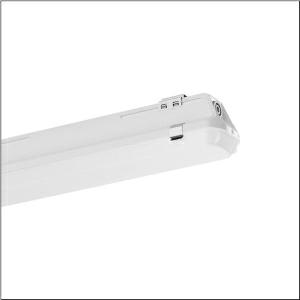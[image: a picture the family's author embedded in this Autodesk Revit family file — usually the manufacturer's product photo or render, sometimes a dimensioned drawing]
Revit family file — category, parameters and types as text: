
# Revit family: monsun_r__11_emergency_51fp20dp467h3h_e354
name_source: partatom
category: Lighting Fixtures
units: mm (PartAtom-declared; Revit-internal decimal feet)

## family parameters
Cut with Voids When Loaded = No
Host = Face
Light Source = No
Part Type = Normal
Room Calculation Point = No
Round Connector Dimension = Use Diameter
Shared = No

## types (1)
- --- (1 x LED, 790 lm, 5 W, 4000K)
    Apparent Load = 5 VA
    CIE Flux Codes = 45 75 93 94 100
    Color Rendering = 80
    Color Temperature = 4000K
    Default Elevation = 1800 mm
    Description = Monsun® 11 emergency, damp-proof luminaire, chain hanger, primary optical cover: enclosure, of PC, light emission: direct distribution, primary light characteristic: symmetric, installation type: suspended mounting, surface-mounted, horizontal mounting, vertical mounting, LED, rated luminous flux: 5.450lm, luminous efficacy: 158lm/W, light colour: 840, colour temperature: 4000K, control gear: ECG DALI, with terminal, 5+3-pole, max. 2.5mm², mains connection: 220..240V, AC, 50/60Hz, rated input power: 35W, control gear: single battery element, battery: NiCd, 4,5Ah, mains connection: 230V, luminaire housing, of glass-fibre reinforced polyester, uncoated, bright grey, incl. chain hanger, length: 1.590mm, width: 90mm, height: 88mm, clip for enclosure, of stainless steel (V2A), ceiling mounting element, of stainless steel (V2A), chain hanger, of stainless steel (V2A), protection rating (complete): IP66, insulation class (complete): insulation class I (protective earthing), certification: CE, UKCA, protection symbol: D, impact resistance: IK08, permissible operating ambient temperature: +5..+35°C, standard: EN 50419, EN 60598-2-1, EN 60598-2-22, no direct snow, no direct sun, no direct rain, for indoor or canopied outdoor use, corresponds to IFS (International Featured Standards) requirements for safety and quality in the food industry, contact your sales advisor before using the luminaires in applications with unclear chemical exposure, large temperature fluctuations or condensation-forming humidity, LABS conformity tested according to VDMA 24364:2018-05, packaging unit: 1 piece
    Height = 89 mm
    Lamp = 1 x LED
    Lamp Light Flux = 790 lm
    Lamp Power = 5 W
    Lamp count = 1
    Length = 1590 mm
    Luminous efficacy = 158 lm/W
    Manufacturer = Siteco
    ModVariant = No
    Model = 51FP20DP467H3H
    Mounting Place = Ceiling
    Mounting Type = Surface mounted
    Number of Poles = 1
    OnlyDefault = Yes
    Power Factor = 1
    Product Name = Monsun® 11 emergency
    Product group = damp-proof luminaire
    ProductGroupID = 300
    Protection Class = Protection class I
    Protection Degree = IP 66
    RLX_Detail_Level = 1
    RLX_Emergency_Light_Flux = 0 lm
    RLX_Emergency_Type = 0
    RLX_Emergency_Type_DB = No
    RlxData = <blob elided: 92545 chars, md5=c2a40069>
    Socket = socket
    Standby Power = 0 W
    System Light Flux = 790 lm
    System Power = 5 W
    Type Comments = : emergency light operation: 3 h
    Type Image = l_1319650.jpg
    URL = http://relux.com
    VarID = @adj_171455
    Voltage = 0 V
    Weight = 0.00 kg
    Width = 90 mm

## geometry (parser evidence)
native form markers: Blend x4, Sweep x11
no freeform markers — native parametric forms only
